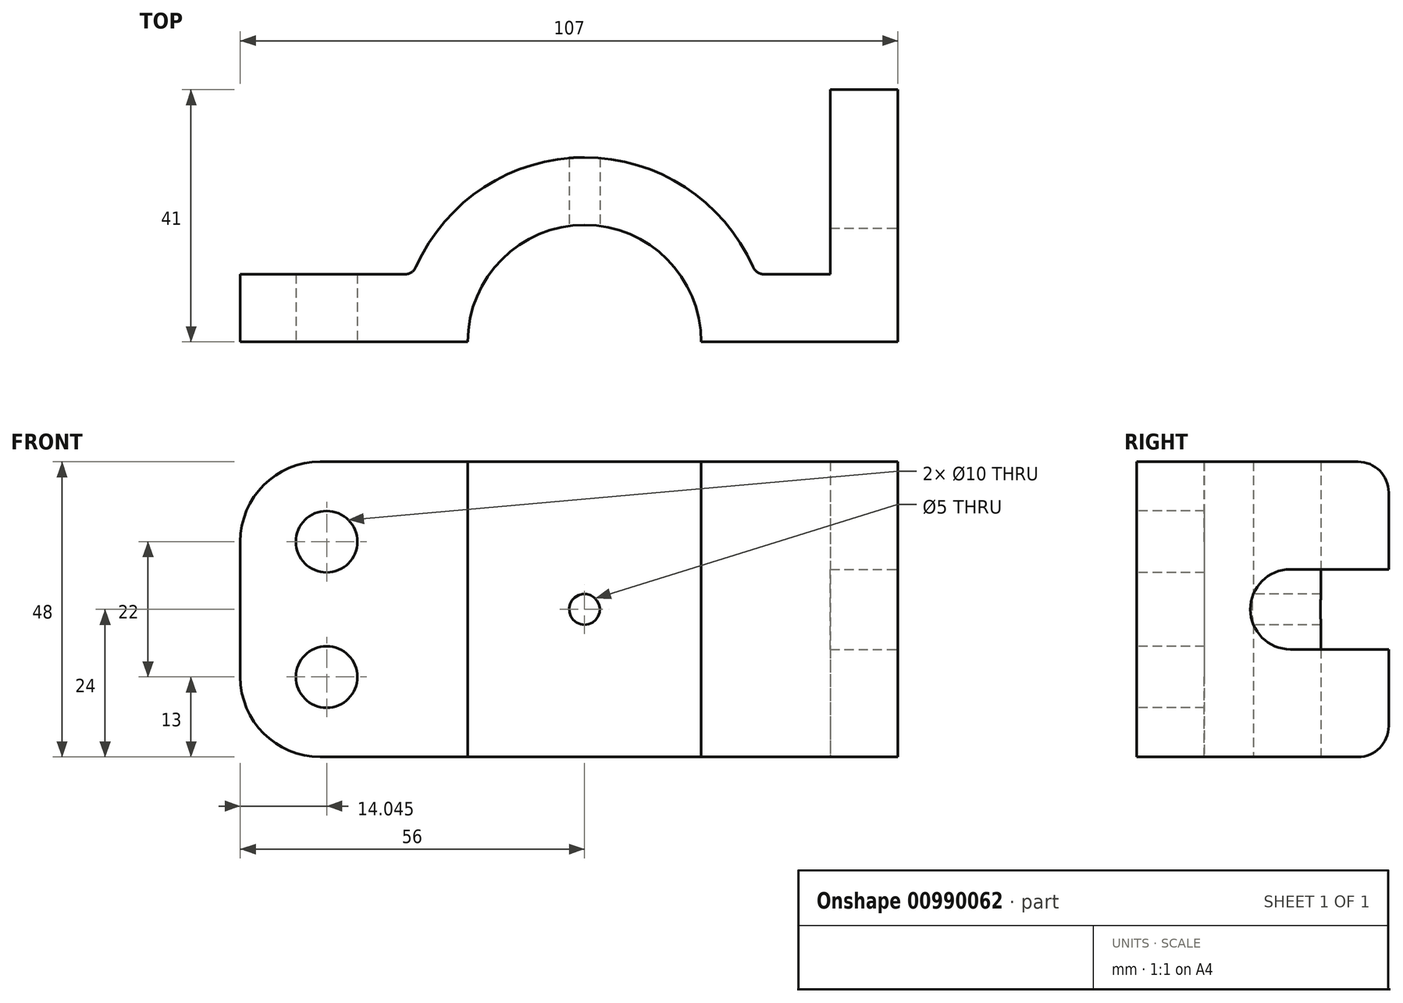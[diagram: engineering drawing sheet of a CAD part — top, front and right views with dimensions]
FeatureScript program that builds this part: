
annotation { "Feature Type Name" : "Feature", "Feature Type Description" : "" }
export const myFeature = defineFeature(function(context is Context, id is Id, definition is map)
    precondition{}
    {
        {
            var Q0;
            Q0=qCreatedBy(makeId("Top.planeOp"),FACE);
            var sketch = newSketch(context, id + "F0", { "sketchPlane" : qUnion([Q0])});
            skCircle(sketch, "E0", {"center": v(0, 0) * mm, "radius": 30 * mm});
            skCircle(sketch, "E1", {"center": v(0, 0) * mm, "radius": 19 * mm});
            skLineSegment(sketch, "E2.bottom", {"start": v(-56, 11) * mm, "end": v(51, 11) * mm});
            skLineSegment(sketch, "E2.top", {"start": v(-56, 0) * mm, "end": v(51, 0) * mm});
            skLineSegment(sketch, "E2.left", {"start": v(-56, 11) * mm, "end": v(-56, 0) * mm});
            skLineSegment(sketch, "E2.right", {"start": v(51, 11) * mm, "end": v(51, 0) * mm});
            skLineSegment(sketch, "E3.bottom", {"start": v(51, 11) * mm, "end": v(40, 11) * mm});
            skLineSegment(sketch, "E3.top", {"start": v(51, 41) * mm, "end": v(40, 41) * mm});
            skLineSegment(sketch, "E3.left", {"start": v(51, 11) * mm, "end": v(51, 41) * mm});
            skLineSegment(sketch, "E3.right", {"start": v(40, 11) * mm, "end": v(40, 41) * mm});
            skSolve(sketch);
        }
        {
            var Q0;
            {var subQ5=sQuery(id+"F0.wireOp",EDGE,"E2.left");Q0=makeQuery(id+"F0.imprint","IMPRINT",FACE,{"disambiguationData":[TD([[makeQuery(id+"F0.imprint","IMPRINT",EDGE,{"derivedFrom":subQ5}),1.0]])]});}
            var Q1;
            {var subQ0=sQuery(id+"F0.wireOp",EDGE,"E2.bottom");var subQ1=sQuery(id+"F0.wireOp",EDGE,"E0");var subQ2=makeQuery(id+"F0.imprint","INTERSECT",VERTEX,{"disambiguationData":[OD(1.0)],"derivedFrom":[subQ1,subQ0]});Q1=makeQuery(id+"F0.imprint","IMPRINT",FACE,{"disambiguationData":[TD([[makeQuery(id+"F0.imprint","IMPRINT",EDGE,{"disambiguationData":[TD([[subQ2,-1.0]])],"derivedFrom":subQ1}),1.0]])]});}
            var Q2;
            {var subQ0=sQuery(id+"F0.wireOp",EDGE,"E2.bottom");var subQ1=sQuery(id+"F0.wireOp",EDGE,"E0");var subQ2=makeQuery(id+"F0.imprint","INTERSECT",VERTEX,{"disambiguationData":[OD(0.0)],"derivedFrom":[subQ1,subQ0]});Q2=makeQuery(id+"F0.imprint","IMPRINT",FACE,{"disambiguationData":[TD([[makeQuery(id+"F0.imprint","IMPRINT",EDGE,{"disambiguationData":[TD([[subQ2,-1.0]])],"derivedFrom":subQ1}),1.0]])]});}
            var Q3;
            {var subQ0=sQuery(id+"F0.wireOp",EDGE,"E2.bottom");var subQ1=sQuery(id+"F0.wireOp",EDGE,"E0");var subQ2=makeQuery(id+"F0.imprint","INTERSECT",VERTEX,{"disambiguationData":[OD(0.0)],"derivedFrom":[subQ1,subQ0]});Q3=makeQuery(id+"F0.imprint","IMPRINT",FACE,{"disambiguationData":[TD([[makeQuery(id+"F0.imprint","IMPRINT",EDGE,{"disambiguationData":[TD([[subQ2,1.0]])],"derivedFrom":subQ1}),1.0]])]});}
            var Q4;
            {var subQ0=sQuery(id+"F0.wireOp",EDGE,"E2.right");Q4=makeQuery(id+"F0.imprint","IMPRINT",FACE,{"disambiguationData":[TD([[makeQuery(id+"F0.imprint","IMPRINT",EDGE,{"derivedFrom":subQ0}),-1.0]])]});}
            var Q5;
            Q5=makeQuery(id+"F0.imprint","IMPRINT",FACE,{"disambiguationData":[TD([[makeQuery(id+"F0.imprint","IMPRINT",EDGE,{"derivedFrom":sQuery(id+"F0.wireOp",EDGE,"E3.top")}),1.0]])]});
            extrude(context, id + "F1", {"entities" : qUnion([Q0, Q1, Q2, Q3, Q4, Q5]), "endBound" : BoundingType.SYMMETRIC, "depth" : 48 * mm, "offsetDistance" : 25 * mm});
        }
        {
            var Q0;
            Q0=makeQuery(id+"F1.opExtrude","SWEPT_FACE",FACE,{"disambiguationData":[OSD([sQuery(id+"F0.wireOp",EDGE,"E2.right"),sQuery(id+"F0.wireOp",EDGE,"E3.left")])]});
            var sketch = newSketch(context, id + "F2", { "sketchPlane" : qUnion([Q0])});
            skLineSegment(sketch, "E4", {"start": v(0, 0) * mm, "end": v(41, 0) * mm, "construction": true});
            skCircle(sketch, "E5", {"center": v(25, 0) * mm, "radius": 6.5 * mm});
            skLineSegment(sketch, "E6", {"start": v(25, 6.5) * mm, "end": v(41, 6.5) * mm});
            skLineSegment(sketch, "E7", {"start": v(25, -6.5) * mm, "end": v(41, -6.5) * mm});
            skSolve(sketch);
        }
        {
            var Q0;
            {var subQ0=sQuery(id+"F2.wireOp",EDGE,"E6");Q0=makeQuery(id+"F2.imprint","IMPRINT",FACE,{"disambiguationData":[TD([[makeQuery(id+"F2.imprint","IMPRINT",EDGE,{"derivedFrom":subQ0}),-1.0]])]});}
            var Q1;
            {var subQ0=sQuery(id+"F2.wireOp",EDGE,"E5");var subQ1=makeQuery(id+"F2.imprint","INTERSECT",VERTEX,{"derivedFrom":[subQ0,sQuery(id+"F2.wireOp",EDGE,"E6")]});Q1=makeQuery(id+"F2.imprint","IMPRINT",FACE,{"disambiguationData":[TD([[makeQuery(id+"F2.imprint","IMPRINT",EDGE,{"disambiguationData":[TD([[subQ1,-1.0]])],"derivedFrom":subQ0}),1.0]])]});}
            var Q2;
            Q2=makeQuery(id+"F1.opExtrude","SWEPT_FACE",FACE,{"disambiguationData":[OSD([sQuery(id+"F0.wireOp",EDGE,"E3.right")])]});
            extrude(context, id + "F3", {"entities" : qUnion([Q0, Q1]), "operationType" : NewBodyOperationType.REMOVE, "endBound" : BoundingType.UP_TO_SURFACE, "oppositeDirection" : true, "depth" : 25 * mm, "endBoundEntityFace" : qUnion([Q2]), "offsetDistance" : 25 * mm});
        }
        {
            var Q0;
            Q0=qCreatedBy(makeId("Front.planeOp"),FACE);
            var sketch = newSketch(context, id + "F4", { "sketchPlane" : qUnion([Q0])});
            skCircle(sketch, "E8", {"center": v(0, 0) * mm, "radius": 2.5 * mm});
            skLineSegment(sketch, "E9", {"start": v(-56, 0) * mm, "end": v(-27.91, 0) * mm, "construction": true});
            skLineSegment(sketch, "E10", {"start": v(-41.96, -24) * mm, "end": v(-41.96, 24) * mm, "construction": true});
            skCircle(sketch, "E11", {"center": v(-41.96, -11) * mm, "radius": 5 * mm});
            skCircle(sketch, "E12", {"center": v(-41.96, 11) * mm, "radius": 5 * mm});
            skSolve(sketch);
        }
        {
            var Q0;
            Q0=makeQuery(id+"F4.imprint","IMPRINT",FACE,{"disambiguationData":[TD([[makeQuery(id+"F4.imprint","IMPRINT",EDGE,{"derivedFrom":sQuery(id+"F4.wireOp",EDGE,"E12")}),1.0]])]});
            var Q1;
            Q1=makeQuery(id+"F4.imprint","IMPRINT",FACE,{"disambiguationData":[TD([[makeQuery(id+"F4.imprint","IMPRINT",EDGE,{"derivedFrom":sQuery(id+"F4.wireOp",EDGE,"E11")}),1.0]])]});
            var Q2;
            Q2=makeQuery(id+"F4.imprint","IMPRINT",FACE,{"disambiguationData":[TD([[makeQuery(id+"F4.imprint","IMPRINT",EDGE,{"derivedFrom":sQuery(id+"F4.wireOp",EDGE,"E8")}),1.0]])]});
            extrude(context, id + "F5", {"entities" : qUnion([Q0, Q1, Q2]), "operationType" : NewBodyOperationType.REMOVE, "endBound" : BoundingType.THROUGH_ALL, "oppositeDirection" : true, "depth" : 25 * mm, "offsetDistance" : 25 * mm});
        }
        {
            var Q0;
            Q0=makeQuery(id+"F1.opExtrude","CAP_EDGE",EDGE,{"disambiguationData":[OSD([sQuery(id+"F0.wireOp",EDGE,"E2.left")])],"isStart":true});
            var Q1;
            Q1=makeQuery(id+"F1.opExtrude","CAP_EDGE",EDGE,{"disambiguationData":[OSD([sQuery(id+"F0.wireOp",EDGE,"E2.left")])],"isStart":false});
            fillet(context, id + "F6", {"entities" : qUnion([Q0, Q1]), "radius" : 13 * mm, "tangentPropagation" : true, "allowEdgeOverflow" : false});
        }
        {
            var Q0;
            Q0=makeQuery(id+"F1.opExtrude","CAP_EDGE",EDGE,{"disambiguationData":[OSD([sQuery(id+"F0.wireOp",EDGE,"E3.top")])],"isStart":true});
            var Q1;
            Q1=makeQuery(id+"F1.opExtrude","CAP_EDGE",EDGE,{"disambiguationData":[OSD([sQuery(id+"F0.wireOp",EDGE,"E3.top")])],"isStart":false});
            fillet(context, id + "F7", {"entities" : qUnion([Q0, Q1]), "radius" : 5 * mm, "tangentPropagation" : true, "allowEdgeOverflow" : false});
        }
        {
            var Q0;
            {var subQ0=sQuery(id+"F0.wireOp",EDGE,"E2.bottom");var subQ1=sQuery(id+"F0.wireOp",EDGE,"E0");Q0=makeQuery(id+"F1.opExtrude","SWEPT_EDGE",EDGE,{"disambiguationData":[OSD([subQ1,subQ0]),TDD([makeQuery(id+"F0.imprint","INTERSECT",VERTEX,{"disambiguationData":[OD(1.0)],"derivedFrom":[subQ1,subQ0]})])]});}
            var Q1;
            {var subQ0=sQuery(id+"F0.wireOp",EDGE,"E2.bottom");var subQ1=sQuery(id+"F0.wireOp",EDGE,"E0");Q1=makeQuery(id+"F1.opExtrude","SWEPT_EDGE",EDGE,{"disambiguationData":[OSD([subQ1,subQ0]),TDD([makeQuery(id+"F0.imprint","INTERSECT",VERTEX,{"disambiguationData":[OD(0.0)],"derivedFrom":[subQ1,subQ0]})])]});}
            fillet(context, id + "F8", {"entities" : qUnion([Q0, Q1]), "radius" : 2 * mm, "tangentPropagation" : true, "allowEdgeOverflow" : false});
        }
    });
